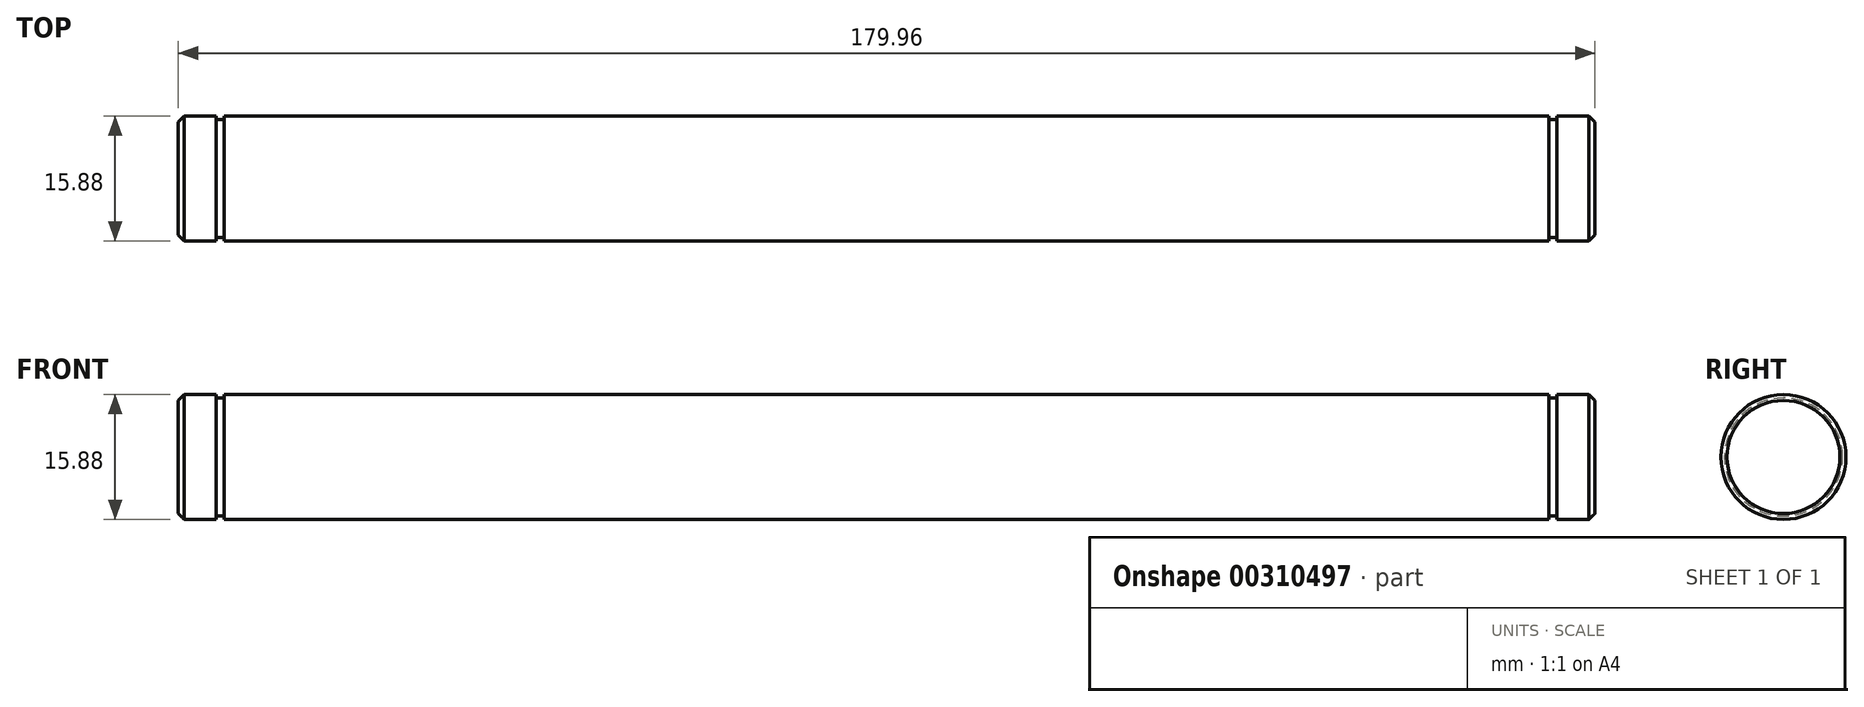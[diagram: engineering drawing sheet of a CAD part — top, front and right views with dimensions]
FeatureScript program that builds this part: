
annotation { "Feature Type Name" : "Feature", "Feature Type Description" : "" }
export const myFeature = defineFeature(function(context is Context, id is Id, definition is map)
    precondition{}
    {
        {
            var Q0;
            Q0=qCreatedBy(makeId("Right.planeOp"),FACE);
            var sketch = newSketch(context, id + "F0", { "sketchPlane" : qUnion([Q0])});
            skCircle(sketch, "E0", {"center": v(0, 0) * mm, "radius": 7.94 * mm});
            skSolve(sketch);
        }
        {
            var Q0;
            Q0=qSketchRegion(id+"F0",true);
            extrude(context, id + "F1", {"entities" : qUnion([Q0]), "endBound" : BoundingType.SYMMETRIC, "depth" : 168.27 * mm});
        }
        {
            var Q0;
            Q0=makeQuery(id+"F1.opExtrude","CAP_FACE",FACE,{"disambiguationData":[OSD([sQuery(id+"F0.wireOp",EDGE,"E0")])],"isStart":false});
            var sketch = newSketch(context, id + "F2", { "sketchPlane" : qUnion([Q0])});
            skCircle(sketch, "E1", {"center": v(0, 0) * mm, "radius": 7.5 * mm});
            skSolve(sketch);
        }
        {
            var Q0;
            Q0=qSketchRegion(id+"F2",true);
            extrude(context, id + "F3", {"entities" : qUnion([Q0]), "depth" : 1.02 * mm});
        }
        {
            var Q0;
            Q0=makeQuery(id+"F3.opExtrude","CAP_FACE",FACE,{"disambiguationData":[OSD([sQuery(id+"F2.wireOp",EDGE,"E1")])],"isStart":false});
            var sketch = newSketch(context, id + "F4", { "sketchPlane" : qUnion([Q0])});
            skCircle(sketch, "E2", {"center": v(0, 0) * mm, "radius": 7.94 * mm});
            skSolve(sketch);
        }
        {
            var Q0;
            Q0=qSketchRegion(id+"F4",true);
            extrude(context, id + "F5", {"entities" : qUnion([Q0]), "operationType" : NewBodyOperationType.ADD, "depth" : 4.83 * mm});
        }
        {
            var Q0;
            Q0=makeQuery(id+"F5.opExtrude","CAP_FACE",FACE,{"disambiguationData":[OSD([sQuery(id+"F4.wireOp",EDGE,"E2")])],"isStart":false});
            chamfer(context, id + "F6", {"entities" : qUnion([Q0]), "width" : 0.76 * mm, "tangentPropagation" : true});
        }
        {
            var Q0;
            Q0=makeQuery(id+"F3.opExtrude","SWEPT_BODY",BODY,{"disambiguationData":[OSD([sQuery(id+"F2.wireOp",EDGE,"E1")])]});
            var Q1;
            Q1=qCreatedBy(makeId("Right.planeOp"),FACE);
            mirror(context, id + "F7", {"operationType" : NewBodyOperationType.ADD, "entities" : qUnion([Q0]), "mirrorPlane" : qUnion([Q1])});
        }
    });
